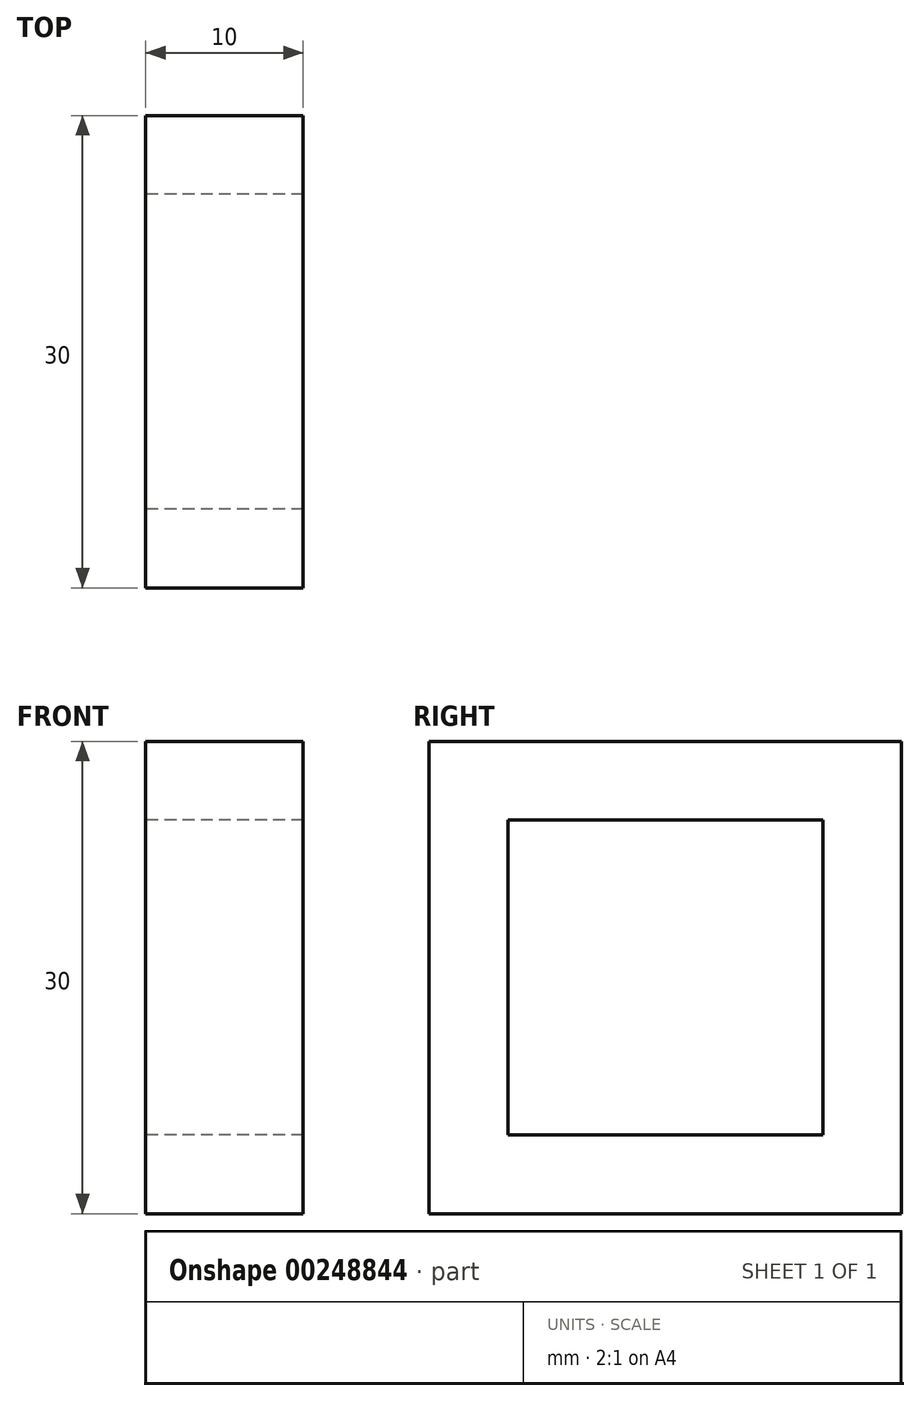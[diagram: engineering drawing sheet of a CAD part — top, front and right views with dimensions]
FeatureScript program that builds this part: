
annotation { "Feature Type Name" : "Feature", "Feature Type Description" : "" }
export const myFeature = defineFeature(function(context is Context, id is Id, definition is map)
    precondition{}
    {
        {
            var Q0;
            Q0=qCreatedBy(makeId("Right.planeOp"),FACE);
            var sketch = newSketch(context, id + "F0", { "sketchPlane" : qUnion([Q0])});
            skLineSegment(sketch, "E0.bottom", {"start": v(-10, 10) * mm, "end": v(10, 10) * mm});
            skLineSegment(sketch, "E0.top", {"start": v(-10, -10) * mm, "end": v(10, -10) * mm});
            skLineSegment(sketch, "E0.left", {"start": v(-10, 10) * mm, "end": v(-10, -10) * mm});
            skLineSegment(sketch, "E0.right", {"start": v(10, 10) * mm, "end": v(10, -10) * mm});
            skPoint(sketch, "E0.middle", {"position": v(0, 0) * mm});
            skLineSegment(sketch, "E1.bottom", {"start": v(15, 15) * mm, "end": v(-15, 15) * mm});
            skLineSegment(sketch, "E1.top", {"start": v(15, -15) * mm, "end": v(-15, -15) * mm});
            skLineSegment(sketch, "E1.left", {"start": v(15, 15) * mm, "end": v(15, -15) * mm});
            skLineSegment(sketch, "E1.right", {"start": v(-15, 15) * mm, "end": v(-15, -15) * mm});
            skSolve(sketch);
        }
        {
            var Q0;
            Q0=makeQuery(id+"F0.imprint","IMPRINT",FACE,{"disambiguationData":[TD([[makeQuery(id+"F0.imprint","IMPRINT",EDGE,{"derivedFrom":sQuery(id+"F0.wireOp",EDGE,"E0.bottom")}),1.0]])]});
            extrude(context, id + "F1", {"entities" : qUnion([Q0]), "endBound" : BoundingType.SYMMETRIC, "depth" : 10 * mm});
        }
    });
